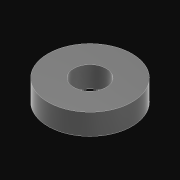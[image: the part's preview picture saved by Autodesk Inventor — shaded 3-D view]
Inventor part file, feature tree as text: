
AUTODESK INVENTOR PART (.ipt)
format: ipt  version: 2021 (Build 250183000, 183)  size: 119,808 bytes
history: native  units: in
note: dims shown in document units (in); Inventor stores cm internally (conversion verified against a paired STEP export)
features: other x9, sketch x1
ambient origin geometry x8: Origin, YZ Plane, XZ Plane, XY Plane, X Axis, Y Axis, Z Axis, Center Point
bodies: Solid1 (feature_tree), Body (feature_tree)
feature tree (10):
  other  "Table"
  other  "NSpacer White .500 OD x .125"
  other  "NSpacer White .500 OD x .250"
  other  "NSpacer White .500 OD x .375"
  other  "NSpacer White .500 OD x .500"
  other  "NSpacer Black .500 OD x .125"
  other  "NSpacer Black .500 OD x .250"
  other  "NSpacer Black .500 OD x .375"
  other  "NSpacer Black .500 OD x .500"
  sketch  "Sketch1"  dims[d0=0.194in d1=0.5in d3=0.0in]
